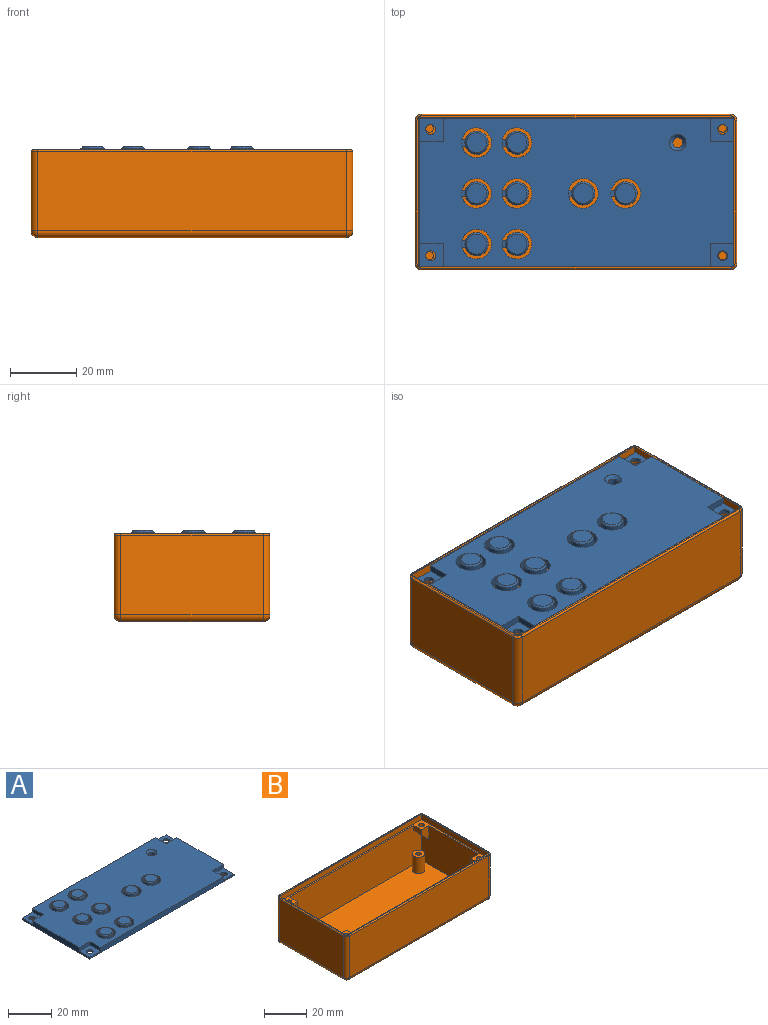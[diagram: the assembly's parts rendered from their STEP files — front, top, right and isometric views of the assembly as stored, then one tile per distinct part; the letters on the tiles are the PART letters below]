
ASSEMBLY  parts=2 mates=1
PART A: 80 faces, bbox 94.6x44.6x4 mm
  f0: plane 94.6x44.6mm, normal (0,0,1), area 3494.6mm2, adj f1,f2,f3,f4,f7,f11,f15,f19
  f1: plane 94.6x3mm, normal (0,-1,0), area 255.8mm2, adj f0,f2,f4,f5,f68,f69,f74,f75
  f2: plane 44.6x3mm, normal (1,0,0), area 105.8mm2, adj f0,f1,f3,f5,f71,f72,f73,f75
  f3: plane 94.6x3mm, normal (0,1,0), area 255.8mm2, adj f0,f2,f4,f5,f65,f66,f70,f72
  f4: plane 44.6x3mm, normal (-1,0,0), area 105.8mm2, adj f0,f1,f3,f5,f64,f66,f67,f69
  f5: plane 94.6x44.6mm, normal (0,0,-1), area 3998.9mm2, adj f1,f2,f3,f4,f6,f7,f8,f9
  f6: plane 1.03x1mm, normal (0,-1,0), area 1mm2, adj f5,f7,f9,f53
  f7: cylinder r=4.5mm len=9mm, axis (0,0,1), area 82.8mm2, adj f0,f5,f6,f8,f53
  f8: plane 1.03x1mm, normal (0,1,0), area 1mm2, adj f5,f7,f9,f53
  f9: cylinder r=3.5mm len=7mm, axis (0,0,1), area 74.9mm2, adj f5,f6,f8,f53,f61
  f10: plane 1.03x1mm, normal (0,-1,0), area 1mm2, adj f5,f11,f13,f52
  f11: cylinder r=4.5mm len=9mm, axis (0,0,1), area 82.8mm2, adj f0,f5,f10,f12,f52
  f12: plane 1.03x1mm, normal (0,1,0), area 1mm2, adj f5,f11,f13,f52
  f13: cylinder r=3.5mm len=7mm, axis (0,0,1), area 74.9mm2, adj f5,f10,f12,f52,f56
  f14: plane 1.03x1mm, normal (0,-1,0), area 1mm2, adj f5,f15,f17,f51
  f15: cylinder r=4.5mm len=9mm, axis (0,0,1), area 82.8mm2, adj f0,f5,f14,f16,f51
  f16: plane 1.03x1mm, normal (0,1,0), area 1mm2, adj f5,f15,f17,f51
  f17: cylinder r=3.5mm len=7mm, axis (0,0,1), area 74.9mm2, adj f5,f14,f16,f51,f57
  f18: plane 1.03x1mm, normal (0,-1,0), area 1mm2, adj f5,f19,f21,f50
  f19: cylinder r=4.5mm len=9mm, axis (0,0,1), area 82.8mm2, adj f0,f5,f18,f20,f50
  f20: plane 1.03x1mm, normal (0,1,0), area 1mm2, adj f5,f19,f21,f50
  f21: cylinder r=3.5mm len=7mm, axis (0,0,1), area 74.9mm2, adj f5,f18,f20,f50,f55
  f22: plane 1.03x1mm, normal (0,-1,0), area 1mm2, adj f5,f23,f25,f49
  f23: cylinder r=4.5mm len=9mm, axis (0,0,1), area 82.8mm2, adj f0,f5,f22,f24,f49
  f24: plane 1.03x1mm, normal (0,1,0), area 1mm2, adj f5,f23,f25,f49
  f25: cylinder r=3.5mm len=7mm, axis (0,0,1), area 74.9mm2, adj f5,f22,f24,f49,f54
  f26: plane 1.03x1mm, normal (0,-1,0), area 1mm2, adj f5,f27,f29,f48
  f27: cylinder r=4.5mm len=9mm, axis (0,0,1), area 82.8mm2, adj f0,f5,f26,f28,f48
  f28: plane 1.03x1mm, normal (0,1,0), area 1mm2, adj f5,f27,f29,f48
  f29: cylinder r=3.5mm len=7mm, axis (0,0,1), area 74.9mm2, adj f5,f26,f28,f48,f58
  f30: plane 1.03x1mm, normal (0,-1,0), area 1mm2, adj f5,f31,f33,f47
  f31: cylinder r=4.5mm len=9mm, axis (0,0,1), area 82.8mm2, adj f0,f5,f30,f32,f47
  f32: plane 1.03x1mm, normal (0,1,0), area 1mm2, adj f5,f31,f33,f47
  f33: cylinder r=3.5mm len=7mm, axis (0,0,1), area 74.9mm2, adj f5,f30,f32,f47,f59
  f34: plane 1.03x1mm, normal (0,-1,0), area 1mm2, adj f5,f35,f37,f46
  f35: cylinder r=4.5mm len=9mm, axis (0,0,1), area 82.8mm2, adj f0,f5,f34,f36,f46
  f36: plane 1.03x1mm, normal (0,1,0), area 1mm2, adj f5,f35,f37,f46
  f37: cylinder r=3.5mm len=7mm, axis (0,0,1), area 74.9mm2, adj f5,f34,f36,f46,f60
  f38: plane 6x6mm, normal (0,0,1), area 28.3mm2, adj f61
  f39: plane 6x6mm, normal (0,0,1), area 28.3mm2, adj f58
  f40: plane 6x6mm, normal (0,0,1), area 28.3mm2, adj f54
  f41: plane 6x6mm, normal (0,0,1), area 28.3mm2, adj f55
  f42: plane 6x6mm, normal (0,0,1), area 28.3mm2, adj f59
  f43: plane 6x6mm, normal (0,0,1), area 28.3mm2, adj f60
  f44: plane 6x6mm, normal (0,0,1), area 28.3mm2, adj f57
  f45: plane 6x6mm, normal (0,0,1), area 28.3mm2, adj f56
  f46: plane 2x1.15mm, normal (0,0,1), area 2mm2, adj f34,f35,f36,f37
  f47: plane 2x1.15mm, normal (0,0,1), area 2mm2, adj f30,f31,f32,f33
  f48: plane 2x1.15mm, normal (0,0,1), area 2mm2, adj f26,f27,f28,f29
  f49: plane 2x1.15mm, normal (0,0,1), area 2mm2, adj f22,f23,f24,f25
  f50: plane 2x1.15mm, normal (0,0,1), area 2mm2, adj f18,f19,f20,f21
  f51: plane 2x1.15mm, normal (0,0,1), area 2mm2, adj f14,f15,f16,f17
  f52: plane 2x1.15mm, normal (0,0,1), area 2mm2, adj f10,f11,f12,f13
  f53: plane 2x1.15mm, normal (0,0,1), area 2mm2, adj f6,f7,f8,f9
  f54: cone r=3mm half-angle=45deg, axis (0,0,-1), area 14.4mm2, adj f25,f40
  f55: cone r=3mm half-angle=45deg, axis (0,0,-1), area 14.4mm2, adj f21,f41
  f56: cone r=3mm half-angle=45deg, axis (0,0,-1), area 14.4mm2, adj f13,f45
  f57: cone r=3mm half-angle=45deg, axis (0,0,-1), area 14.4mm2, adj f17,f44
  f58: cone r=3mm half-angle=45deg, axis (0,0,-1), area 14.4mm2, adj f29,f39
  f59: cone r=3mm half-angle=45deg, axis (0,0,-1), area 14.4mm2, adj f33,f42
  f60: cone r=3mm half-angle=45deg, axis (0,0,-1), area 14.4mm2, adj f37,f43
  f61: cone r=3mm half-angle=45deg, axis (0,0,-1), area 14.4mm2, adj f9,f38
  f62: cylinder r=1.5mm len=3mm, axis (0,0,1), area 18.8mm2, adj f5,f63
  f63: cone r=1.5mm half-angle=45deg, axis (0,0,1), area 17.8mm2, adj f0,f62
  f64: plane 7x2mm, normal (0,1,0), area 14mm2, adj f0,f4,f65,f66
  f65: plane 7x2mm, normal (-1,0,0), area 14mm2, adj f0,f3,f64,f66
  f66: plane 7x7mm, normal (0,0,1), area 41.9mm2, adj f3,f4,f64,f65,f76
  f67: plane 7x2mm, normal (0,-1,0), area 14mm2, adj f0,f4,f68,f69
  f68: plane 7x2mm, normal (-1,0,0), area 14mm2, adj f0,f1,f67,f69
  f69: plane 7x7mm, normal (0,0,1), area 41.9mm2, adj f1,f4,f67,f68,f77
  f70: plane 7x2mm, normal (1,0,0), area 14mm2, adj f0,f3,f71,f72
  f71: plane 7x2mm, normal (0,1,0), area 14mm2, adj f0,f2,f70,f72
  f72: plane 7x7mm, normal (0,0,1), area 41.9mm2, adj f2,f3,f70,f71,f78
  f73: plane 7x2mm, normal (0,-1,0), area 14mm2, adj f0,f2,f74,f75
  f74: plane 7x2mm, normal (1,0,0), area 14mm2, adj f0,f1,f73,f75
  f75: plane 7x7mm, normal (0,0,1), area 41.9mm2, adj f1,f2,f73,f74,f79
  f76: cylinder r=1.5mm len=3mm, axis (0,0,1), area 9.4mm2, adj f5,f66
  f77: cylinder r=1.5mm len=3mm, axis (0,0,1), area 9.4mm2, adj f5,f69
  f78: cylinder r=1.5mm len=3mm, axis (0,0,1), area 9.4mm2, adj f5,f72
  f79: cylinder r=1.5mm len=3mm, axis (0,0,1), area 9.4mm2, adj f5,f75
PART B: 68 faces, bbox 97.9x47.9x27 mm
  f0: plane 96x46mm, normal (0,0,1), area 139.1mm2, adj f9,f10,f11,f12,f48,f49,f50,f51
  f1: plane 43x22.5mm, normal (-1,0,0), area 887.5mm2, adj f2,f3,f13,f15,f19,f21,f26,f27
  f2: plane 93x22.5mm, normal (0,1,0), area 2037.5mm2, adj f1,f3,f14,f15,f22,f23,f25,f26
  f3: plane 95x45mm, normal (0,0,1), area 356.4mm2, adj f1,f2,f9,f10,f11,f12,f13,f14
  f4: plane 93x24mm, normal (0,-1,0), area 2232mm2, adj f48,f56,f58,f65
  f5: plane 43x24mm, normal (1,0,0), area 1032mm2, adj f49,f54,f56,f61
  f6: plane 93x24mm, normal (0,1,0), area 2232mm2, adj f51,f52,f54,f62
  f7: plane 43x24mm, normal (-1,0,0), area 1032mm2, adj f50,f52,f58,f66
  f8: plane 93x43mm, normal (0,0,-1), area 3999mm2, adj f61,f62,f65,f66
  f9: plane 95x3mm, normal (0,1,0), area 285mm2, adj f0,f3,f10,f12
  f10: plane 45x3mm, normal (-1,0,0), area 135mm2, adj f0,f3,f9,f11
  f11: plane 95x3mm, normal (0,-1,0), area 285mm2, adj f0,f3,f10,f12
  f12: plane 45x3mm, normal (1,0,0), area 135mm2, adj f0,f3,f9,f11
  f13: plane 93x22.5mm, normal (0,-1,0), area 2037.5mm2, adj f1,f3,f14,f15,f16,f17,f19,f20
  f14: plane 43x22.5mm, normal (1,0,0), area 887.5mm2, adj f2,f3,f13,f15,f17,f18,f23,f24
  f15: plane 93x43mm, normal (0,0,1), area 3885.9mm2, adj f1,f2,f13,f14,f32,f34,f36,f38
  f16: plane 5x3mm, normal (1,0,0), area 15mm2, adj f3,f13,f17,f18
  f17: plane 5x5mm, normal (0.71,0,-0.71), area 28.4mm2, adj f13,f14,f16,f18,f31
  f18: plane 8x5mm, normal (0,-1,0), area 27.5mm2, adj f3,f14,f16,f17
  f19: plane 5.53x5.53mm, normal (-0.71,0,-0.71), area 28.4mm2, adj f1,f13,f20,f21,f30
  f20: plane 5x3mm, normal (-1,0,0), area 15mm2, adj f3,f13,f19,f21
  f21: plane 8x5mm, normal (0,-1,0), area 27.5mm2, adj f1,f3,f19,f20
  f22: plane 5x3mm, normal (1,0,0), area 15mm2, adj f2,f3,f23,f24
  f23: plane 5x5mm, normal (0.71,0,-0.71), area 28.4mm2, adj f2,f14,f22,f24,f29
  f24: plane 8x5mm, normal (0,1,0), area 27.5mm2, adj f3,f14,f22,f23
  f25: plane 5x3mm, normal (-1,0,0), area 15mm2, adj f2,f3,f26,f27
  f26: plane 5.53x5.53mm, normal (-0.71,0,-0.71), area 28.4mm2, adj f1,f2,f25,f27,f28
  f27: plane 8x5mm, normal (0,1,0), area 27.5mm2, adj f1,f3,f25,f26
  f28: cylinder r=1.25mm len=7mm, axis (0,0,1), area 45.2mm2, adj f3,f26
  f29: cylinder r=1.25mm len=7.02mm, axis (0,0,1), area 45.2mm2, adj f3,f23
  f30: cylinder r=1.25mm len=7mm, axis (0,0,1), area 45.2mm2, adj f3,f19
  f31: cylinder r=1.25mm len=7.02mm, axis (0,0,1), area 45.2mm2, adj f3,f17
  f32: cylinder r=3mm len=9.3mm, axis (0,0,-1), area 175.3mm2, adj f15,f33
  f33: plane 6x6mm, normal (0,0,1), area 23.4mm2, adj f32,f42
  f34: cylinder r=3mm len=9.3mm, axis (0,0,-1), area 175.3mm2, adj f15,f35
  f35: plane 6x6mm, normal (0,0,1), area 23.4mm2, adj f34,f40
  f36: cylinder r=3mm len=9.3mm, axis (0,0,-1), area 175.3mm2, adj f15,f37
  f37: plane 6x6mm, normal (0,0,1), area 23.4mm2, adj f36,f44
  f38: cylinder r=3mm len=9.3mm, axis (0,0,-1), area 175.3mm2, adj f15,f39
  f39: plane 6x6mm, normal (0,0,1), area 23.4mm2, adj f38,f46
  f40: cylinder r=1.25mm len=8mm, axis (0,0,1), area 62.8mm2, adj f35,f41
  f41: plane 2.5x2.5mm, normal (0,0,1), area 4.9mm2, adj f40
  f42: cylinder r=1.25mm len=8mm, axis (0,0,1), area 62.8mm2, adj f33,f43
  f43: plane 2.5x2.5mm, normal (0,0,1), area 4.9mm2, adj f42
  f44: cylinder r=1.25mm len=8mm, axis (0,0,1), area 62.8mm2, adj f37,f45
  f45: plane 2.5x2.5mm, normal (0,0,1), area 4.9mm2, adj f44
  f46: cylinder r=1.25mm len=8mm, axis (0,0,1), area 62.8mm2, adj f39,f47
  f47: plane 2.5x2.5mm, normal (0,0,1), area 4.9mm2, adj f46
  f48: cylinder r=0.5mm len=93mm, axis (-1,0,0), area 73mm2, adj f0,f4,f57,f59
  f49: cylinder r=0.5mm len=43mm, axis (0,-1,0), area 33.8mm2, adj f0,f5,f55,f57
  f50: cylinder r=0.5mm len=43mm, axis (0,1,0), area 33.8mm2, adj f0,f7,f53,f59
  f51: cylinder r=0.5mm len=93mm, axis (1,0,0), area 73mm2, adj f0,f6,f53,f55
  f52: cylinder r=2mm len=24mm, axis (0,0,1), area 75.4mm2, adj f6,f7,f53,f64
  f53: torus R=1.5mm, axis (0,0,1), area 2.2mm2, adj f0,f50,f51,f52
  f54: cylinder r=2mm len=24mm, axis (0,0,-1), area 75.4mm2, adj f5,f6,f55,f60
  f55: torus R=1.5mm, axis (0,0,1), area 2.2mm2, adj f0,f49,f51,f54
  f56: cylinder r=2mm len=24mm, axis (0,0,1), area 75.4mm2, adj f4,f5,f57,f63
  f57: torus R=1.5mm, axis (0,0,1), area 2.2mm2, adj f0,f48,f49,f56
  f58: cylinder r=2mm len=24mm, axis (0,0,-1), area 75.4mm2, adj f4,f7,f59,f67
  f59: torus R=1.5mm, axis (0,0,1), area 2.2mm2, adj f0,f48,f50,f58
  f60: sphere r=2mm, area 6.3mm2, adj f54,f61,f62
  f61: cylinder r=2mm len=43mm, axis (0,1,0), area 135.1mm2, adj f5,f8,f60,f63
  f62: cylinder r=2mm len=93mm, axis (-1,0,0), area 292.2mm2, adj f6,f8,f60,f64
  f63: sphere r=2mm, area 6.3mm2, adj f56,f61,f65
  f64: sphere r=2mm, area 6.3mm2, adj f52,f62,f66
  f65: cylinder r=2mm len=93mm, axis (1,0,0), area 292.2mm2, adj f4,f8,f63,f67
  f66: cylinder r=2mm len=43mm, axis (0,-1,0), area 135.1mm2, adj f7,f8,f64,f67
  f67: sphere r=2mm, area 6.3mm2, adj f58,f65,f66
PLACE A t=(-27.52,-23.39,12.72)mm
PLACE B t=(-27.72,-23.19,-10.78)mm fixed
MATE slider A.f79 <-> B.f28  axis (0,0,1) through (16.53,-42.44,13.72)mm
